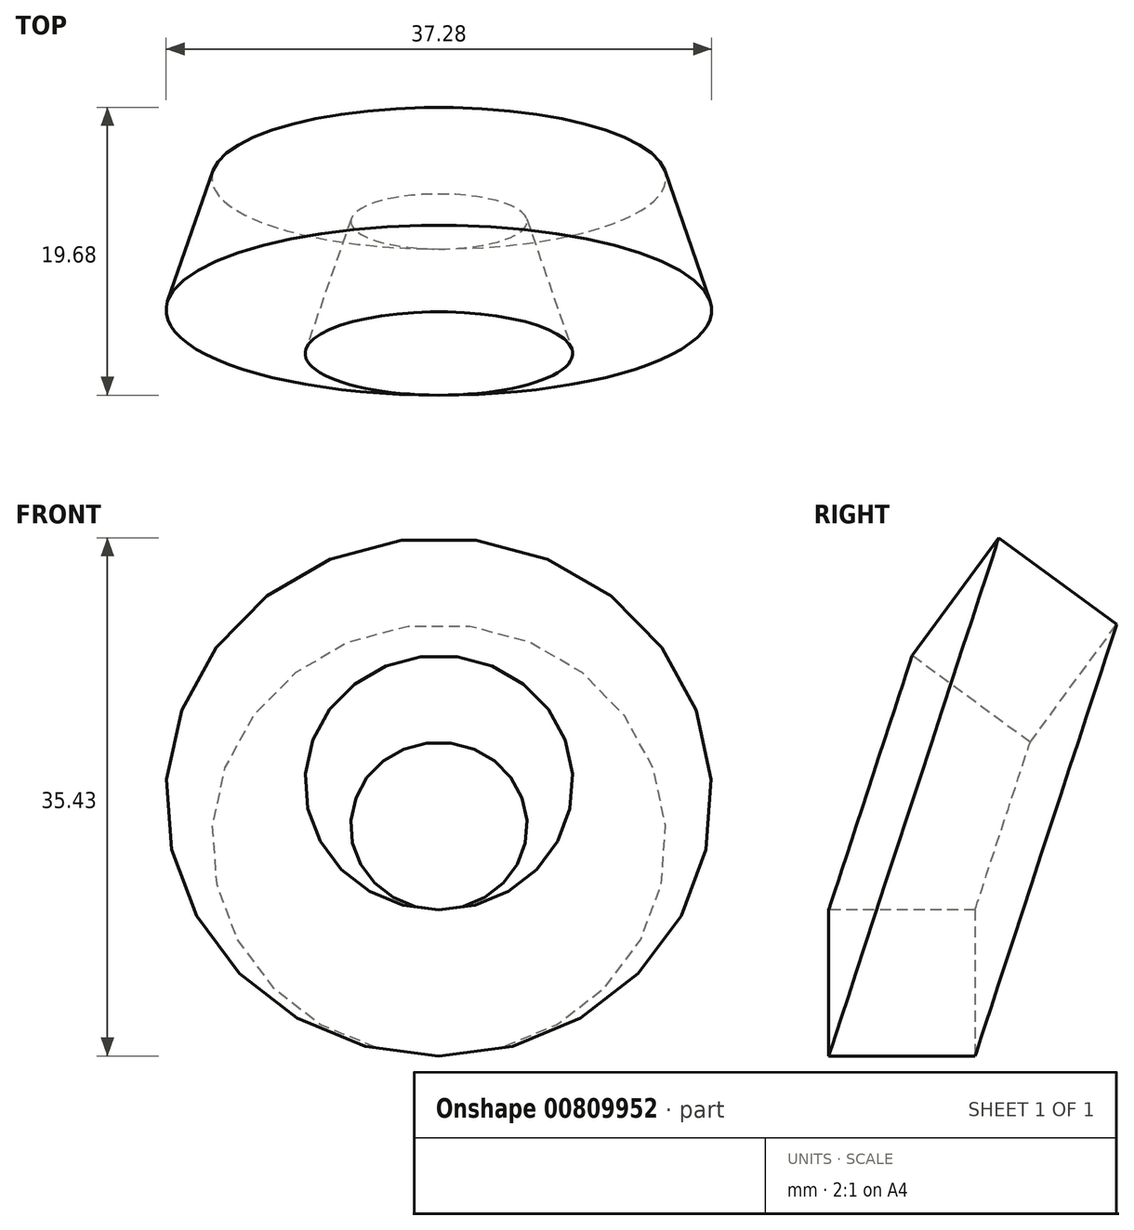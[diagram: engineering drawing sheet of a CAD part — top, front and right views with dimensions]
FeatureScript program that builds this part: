
annotation { "Feature Type Name" : "Feature", "Feature Type Description" : "" }
export const myFeature = defineFeature(function(context is Context, id is Id, definition is map)
    precondition{}
    {
        {
            var Q0;
            Q0=qCreatedBy(makeId("Right.planeOp"),FACE);
            var sketch = newSketch(context, id + "F0", { "sketchPlane" : qUnion([Q0])});
            skLineSegment(sketch, "E0.bottom", {"start": v(-5, 5) * mm, "end": v(5, 5) * mm});
            skLineSegment(sketch, "E0.top", {"start": v(-5, -5) * mm, "end": v(5, -5) * mm});
            skLineSegment(sketch, "E0.left", {"start": v(-5, 5) * mm, "end": v(-5, -5) * mm});
            skLineSegment(sketch, "E0.right", {"start": v(5, 5) * mm, "end": v(5, -5) * mm});
            skPoint(sketch, "E0.middle", {"position": v(0, 0) * mm});
            skLineSegment(sketch, "E1", {"start": v(-50.82, 29.65) * mm, "end": v(39.59, 0) * mm, "construction": true});
            skSolve(sketch);
        }
        {
            var Q0;
            Q0=makeQuery(id+"F0.imprint","IMPRINT",FACE,{"disambiguationData":[TD([[makeQuery(id+"F0.imprint","IMPRINT",EDGE,{"derivedFrom":sQuery(id+"F0.wireOp",EDGE,"E0.bottom")}),-1.0]])]});
            var Q1;
            Q1=sQuery(id+"F0.wireOp",EDGE,"E1");
            revolve(context, id + "F1", {"surfaceOperationType" : NewSurfaceOperationType.NEW, "entities" : qUnion([Q0]), "axis" : qUnion([Q1]), "revolveType" : RevolveType.FULL});
        }
    });
